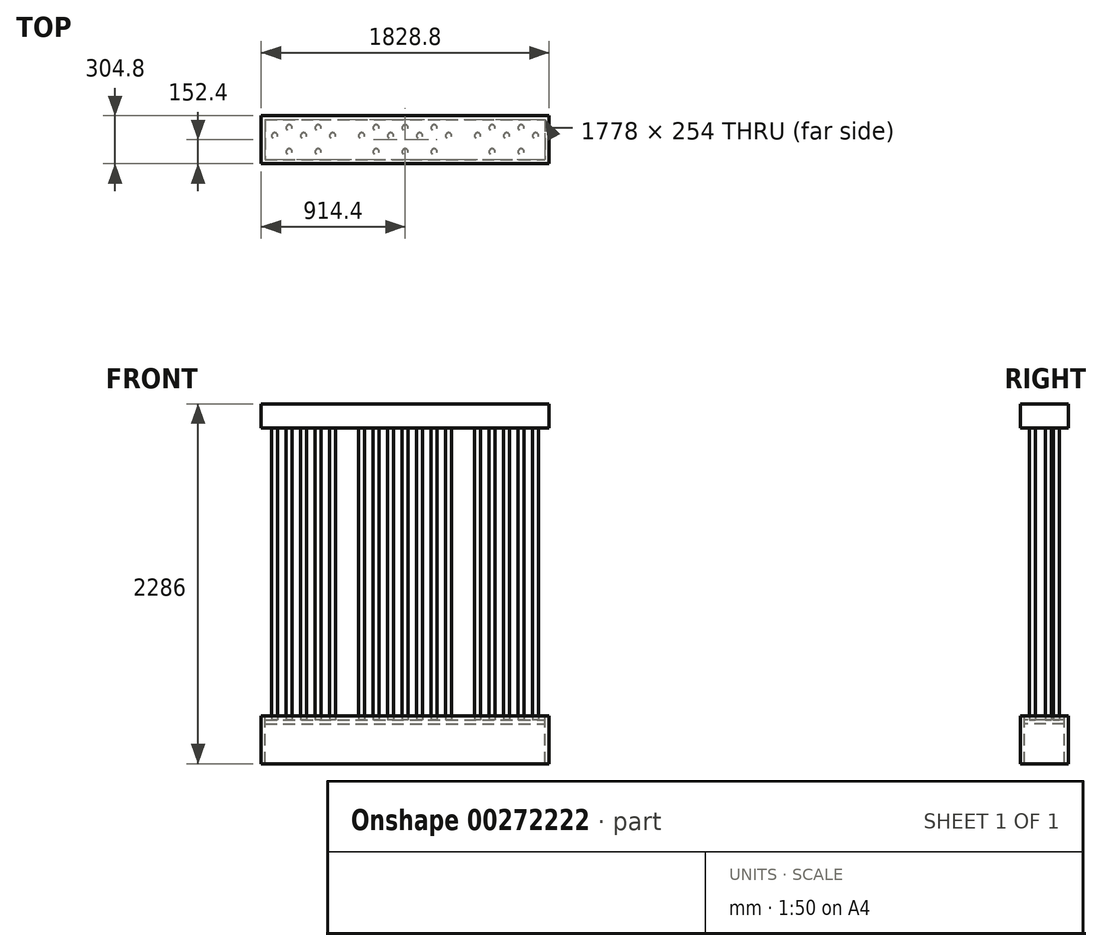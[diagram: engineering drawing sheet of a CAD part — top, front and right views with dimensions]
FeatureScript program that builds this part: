
annotation { "Feature Type Name" : "Feature", "Feature Type Description" : "" }
export const myFeature = defineFeature(function(context is Context, id is Id, definition is map)
    precondition{}
    {
        {
            var Q0;
            Q0=qCreatedBy(makeId("Top.planeOp"),FACE);
            var sketch = newSketch(context, id + "F0", { "sketchPlane" : qUnion([Q0])});
            skLineSegment(sketch, "E0.bottom", {"start": v(-914.4, 152.4) * mm, "end": v(914.4, 152.4) * mm});
            skLineSegment(sketch, "E0.top", {"start": v(-914.4, -152.4) * mm, "end": v(914.4, -152.4) * mm});
            skLineSegment(sketch, "E0.left", {"start": v(-914.4, 152.4) * mm, "end": v(-914.4, -152.4) * mm});
            skLineSegment(sketch, "E0.right", {"start": v(914.4, 152.4) * mm, "end": v(914.4, -152.4) * mm});
            skPoint(sketch, "E0.middle", {"position": v(0, 0) * mm});
            skLineSegment(sketch, "E1.bottom", {"start": v(-889, 127) * mm, "end": v(889, 127) * mm});
            skLineSegment(sketch, "E1.top", {"start": v(-889, -127) * mm, "end": v(889, -127) * mm});
            skLineSegment(sketch, "E1.left", {"start": v(-889, 127) * mm, "end": v(-889, -127) * mm});
            skLineSegment(sketch, "E1.right", {"start": v(889, 127) * mm, "end": v(889, -127) * mm});
            skSolve(sketch);
        }
        {
            var Q0;
            Q0=qCreatedBy(makeId("Top.planeOp"),FACE);
            var sketch = newSketch(context, id + "F1", { "sketchPlane" : qUnion([Q0])});
            skCircle(sketch, "E2", {"center": v(0, 76.2) * mm, "radius": 19.05 * mm});
            skCircle(sketch, "E3", {"center": v(0, -76.2) * mm, "radius": 19.05 * mm});
            skCircle(sketch, "E4.1.0.0", {"center": v(184.15, 76.2) * mm, "radius": 19.05 * mm});
            skCircle(sketch, "E4.1.0.1", {"center": v(184.15, -76.2) * mm, "radius": 19.05 * mm});
            skCircle(sketch, "E4.3.0.0", {"center": v(552.45, 76.2) * mm, "radius": 19.05 * mm});
            skCircle(sketch, "E4.3.0.1", {"center": v(552.45, -76.2) * mm, "radius": 19.05 * mm});
            skCircle(sketch, "E4.4.0.0", {"center": v(736.6, 76.2) * mm, "radius": 19.05 * mm});
            skCircle(sketch, "E4.4.0.1", {"center": v(736.6, -76.2) * mm, "radius": 19.05 * mm});
            skLineSegment(sketch, "E4.direction1", {"start": v(0, 76.2) * mm, "end": v(184.15, 76.2) * mm, "construction": true});
            skCircle(sketch, "E5.1.0.0", {"center": v(-184.15, 76.2) * mm, "radius": 19.05 * mm});
            skCircle(sketch, "E5.1.0.1", {"center": v(-184.15, -76.2) * mm, "radius": 19.05 * mm});
            skCircle(sketch, "E5.3.0.0", {"center": v(-552.45, 76.2) * mm, "radius": 19.05 * mm});
            skCircle(sketch, "E5.3.0.1", {"center": v(-552.45, -76.2) * mm, "radius": 19.05 * mm});
            skCircle(sketch, "E5.4.0.0", {"center": v(-736.6, 76.2) * mm, "radius": 19.05 * mm});
            skCircle(sketch, "E5.4.0.1", {"center": v(-736.6, -76.2) * mm, "radius": 19.05 * mm});
            skLineSegment(sketch, "E5.direction1", {"start": v(0, 76.2) * mm, "end": v(-184.15, 76.2) * mm, "construction": true});
            skCircle(sketch, "E6", {"center": v(92.08, 25.4) * mm, "radius": 19.05 * mm});
            skCircle(sketch, "E7", {"center": v(-92.08, 25.4) * mm, "radius": 19.05 * mm});
            skCircle(sketch, "E8.1.0.0", {"center": v(276.23, 25.4) * mm, "radius": 19.05 * mm});
            skCircle(sketch, "E8.2.0.0", {"center": v(460.38, 25.4) * mm, "radius": 19.05 * mm});
            skLineSegment(sketch, "E8.direction1", {"start": v(92.08, 25.4) * mm, "end": v(276.23, 25.4) * mm, "construction": true});
            skCircle(sketch, "E9.0.3.0", {"center": v(644.52, 25.4) * mm, "radius": 19.05 * mm});
            skCircle(sketch, "E10.0.4.0", {"center": v(828.67, 25.4) * mm, "radius": 19.05 * mm});
            skCircle(sketch, "E11.1.0.0", {"center": v(-276.23, 25.4) * mm, "radius": 19.05 * mm});
            skCircle(sketch, "E11.2.0.0", {"center": v(-460.38, 25.4) * mm, "radius": 19.05 * mm});
            skCircle(sketch, "E11.3.0.0", {"center": v(-644.52, 25.4) * mm, "radius": 19.05 * mm});
            skCircle(sketch, "E11.4.0.0", {"center": v(-828.67, 25.4) * mm, "radius": 19.05 * mm});
            skLineSegment(sketch, "E11.direction1", {"start": v(-92.08, 25.4) * mm, "end": v(-276.23, 25.4) * mm, "construction": true});
            skSolve(sketch);
        }
        {
            var Q0;
            Q0=makeQuery(id+"F0.imprint","IMPRINT",FACE,{"disambiguationData":[TD([[makeQuery(id+"F0.imprint","IMPRINT",EDGE,{"derivedFrom":sQuery(id+"F0.wireOp",EDGE,"E0.bottom")}),-1.0]])]});
            extrude(context, id + "F2", {"entities" : qUnion([Q0]), "oppositeDirection" : true, "depth" : 304.8 * mm});
        }
        {
            var Q0;
            Q0=qCreatedBy(makeId("Top.planeOp"),FACE);
            cPlane(context, id + "F3", {"entities" : qUnion([Q0]), "cplaneType" : CPlaneType.OFFSET, "offset" : 25.4 * mm, "oppositeDirection" : true, "width" : 152.4 * mm, "height" : 152.4 * mm});
        }
        {
            var Q0;
            Q0=qCreatedBy(id+"F3.planeOp",FACE);
            var sketch = newSketch(context, id + "F4", { "sketchPlane" : qUnion([Q0])});
            skLineSegment(sketch, "E12.bottom", {"start": v(-889, 127) * mm, "end": v(889, 127) * mm});
            skLineSegment(sketch, "E12.top", {"start": v(-889, -127) * mm, "end": v(889, -127) * mm});
            skLineSegment(sketch, "E12.left", {"start": v(-889, 127) * mm, "end": v(-889, -127) * mm});
            skLineSegment(sketch, "E12.right", {"start": v(889, 127) * mm, "end": v(889, -127) * mm});
            skPoint(sketch, "E12.middle", {"position": v(0, 0) * mm});
            skSolve(sketch);
        }
        {
            var Q0;
            Q0=makeQuery(id+"F4.imprint","IMPRINT",FACE,{"disambiguationData":[TD([[makeQuery(id+"F4.imprint","IMPRINT",EDGE,{"derivedFrom":sQuery(id+"F4.wireOp",EDGE,"E12.bottom")}),-1.0]])]});
            extrude(context, id + "F5", {"entities" : qUnion([Q0]), "oppositeDirection" : true, "depth" : 25.4 * mm});
        }
        {
            var Q0;
            Q0 = qSketchRegion(id + "F1", true);
            extrude(context, id + "F6", {"entities" : qUnion([Q0]), "operationType" : NewBodyOperationType.ADD, "depth" : 1828.8 * mm, "hasSecondDirection" : true, "secondDirectionOppositeDirection" : true, "secondDirectionDepth" : 50.8 * mm});
        }
        {
            var Q0;
            Q0=makeQuery(id+"F6.opExtrude","CAP_FACE",FACE,{"disambiguationData":[OSD([sQuery(id+"F1.wireOp",EDGE,"E11.4.0.0")])],"isStart":false});
            var sketch = newSketch(context, id + "F7", { "sketchPlane" : qUnion([Q0])});
            skLineSegment(sketch, "E13.bottom", {"start": v(-914.4, 152.4) * mm, "end": v(914.4, 152.4) * mm});
            skLineSegment(sketch, "E13.top", {"start": v(-914.4, -152.4) * mm, "end": v(914.4, -152.4) * mm});
            skLineSegment(sketch, "E13.left", {"start": v(-914.4, 152.4) * mm, "end": v(-914.4, -152.4) * mm});
            skLineSegment(sketch, "E13.right", {"start": v(914.4, 152.4) * mm, "end": v(914.4, -152.4) * mm});
            skPoint(sketch, "E13.middle", {"position": v(0, 0) * mm});
            skSolve(sketch);
        }
        {
            var Q0;
            Q0=makeQuery(id+"F7.imprint","IMPRINT",FACE,{"disambiguationData":[TD([[makeQuery(id+"F7.imprint","IMPRINT",EDGE,{"derivedFrom":sQuery(id+"F7.wireOp",EDGE,"E13.bottom")}),-1.0]])]});
            var Q1;
            Q1=makeQuery(id+"F7.imprint","IMPRINT",FACE,{"disambiguationData":[TD([[makeQuery(id+"F7.imprint","IMPRINT",EDGE,{"derivedFrom":makeQuery(id+"F6.opExtrude","CAP_EDGE",EDGE,{"disambiguationData":[OSD([sQuery(id+"F1.wireOp",EDGE,"E11.4.0.0")])],"isStart":false})}),1.0]])]});
            extrude(context, id + "F8", {"entities" : qUnion([Q0, Q1]), "depth" : 152.4 * mm});
        }
    });
